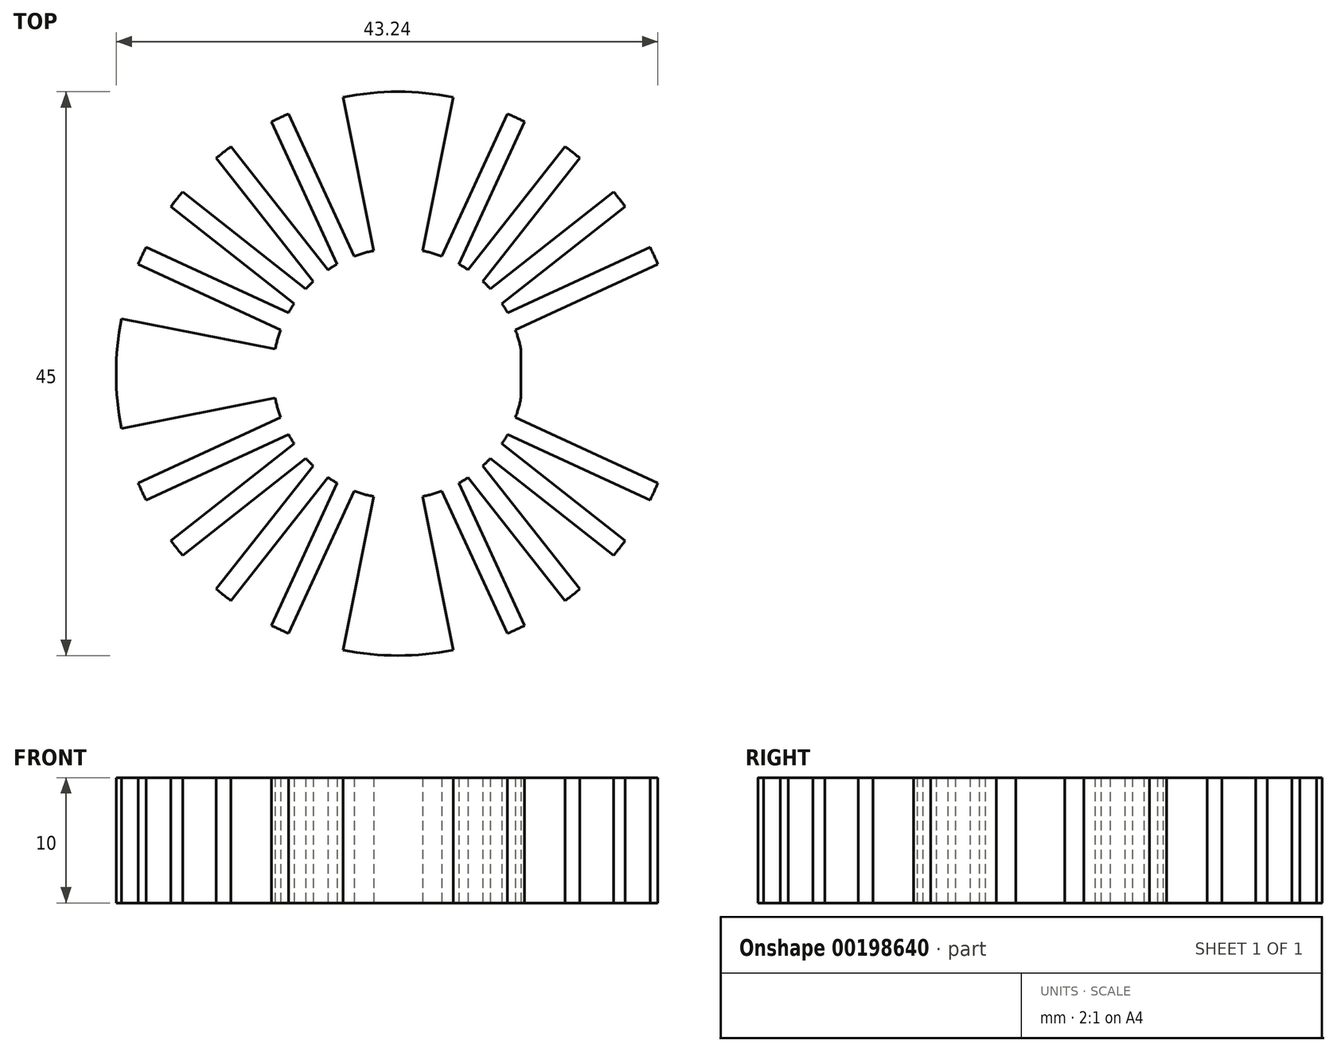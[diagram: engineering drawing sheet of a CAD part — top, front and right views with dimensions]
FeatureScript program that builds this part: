
annotation { "Feature Type Name" : "Feature", "Feature Type Description" : "" }
export const myFeature = defineFeature(function(context is Context, id is Id, definition is map)
    precondition{}
    {
        {
            var Q0;
            Q0=qCreatedBy(makeId("Top.planeOp"),FACE);
            var sketch = newSketch(context, id + "F0", { "sketchPlane" : qUnion([Q0])});
            skArc(sketch, "E0", {"start": v(4.39, 22.07) * mm, "mid": v(0, 22.5) * mm, "end": v(-4.39, 22.07) * mm});
            skArc(sketch, "E1", {"start": v(-1.95, 9.8) * mm, "mid": v(-2.73, 9.62) * mm, "end": v(-3.5, 9.37) * mm});
            skLineSegment(sketch, "E2", {"start": v(1.95, 9.8) * mm, "end": v(4.39, 22.07) * mm});
            skLineSegment(sketch, "E3", {"start": v(4.39, 22.07) * mm, "end": v(1.95, 9.8) * mm});
            skLineSegment(sketch, "E4", {"start": v(-1.95, 9.8) * mm, "end": v(-4.39, 22.07) * mm});
            skLineSegment(sketch, "E5.1.0", {"start": v(-22.07, 4.39) * mm, "end": v(-9.8, 1.95) * mm});
            skLineSegment(sketch, "E5.1.1", {"start": v(-9.8, -1.95) * mm, "end": v(-22.07, -4.39) * mm});
            skLineSegment(sketch, "E5.2.0", {"start": v(-4.39, -22.07) * mm, "end": v(-1.95, -9.8) * mm});
            skLineSegment(sketch, "E5.2.1", {"start": v(1.95, -9.8) * mm, "end": v(4.39, -22.07) * mm});
            skLineSegment(sketch, "E5.3.0", {"start": v(22.07, -4.39) * mm, "end": v(9.8, -1.95) * mm});
            skLineSegment(sketch, "E5.3.1", {"start": v(9.8, 1.95) * mm, "end": v(22.07, 4.39) * mm});
            skLineSegment(sketch, "E6", {"start": v(0, 0) * mm, "end": v(9.42, 20.43) * mm, "construction": true});
            skLineSegment(sketch, "E7", {"start": v(9.42, 20.43) * mm, "end": v(13.93, 17.67) * mm, "construction": true});
            skLineSegment(sketch, "E8", {"start": v(13.93, 17.67) * mm, "end": v(0, 0) * mm, "construction": true});
            skLineSegment(sketch, "E9", {"start": v(4.39, 22.07) * mm, "end": v(9.42, 20.43) * mm, "construction": true});
            skLineSegment(sketch, "E10", {"start": v(0, 0) * mm, "end": v(17.67, 13.93) * mm, "construction": true});
            skLineSegment(sketch, "E11", {"start": v(17.67, 13.93) * mm, "end": v(13.93, 17.67) * mm, "construction": true});
            skLineSegment(sketch, "E12", {"start": v(0, 0) * mm, "end": v(20.43, 9.42) * mm, "construction": true});
            skLineSegment(sketch, "E13", {"start": v(20.43, 9.42) * mm, "end": v(17.67, 13.93) * mm, "construction": true});
            skLineSegment(sketch, "E14", {"start": v(20.43, 9.42) * mm, "end": v(22.07, 4.39) * mm, "construction": true});
            skLineSegment(sketch, "E15", {"start": v(3.5, 9.37) * mm, "end": v(8.73, 20.74) * mm});
            skLineSegment(sketch, "E16.MirrorCS", {"start": v(4.86, 8.74) * mm, "end": v(10.1, 20.1) * mm});
            skLineSegment(sketch, "E17.1.0", {"start": v(5.58, 8.3) * mm, "end": v(13.33, 18.12) * mm});
            skLineSegment(sketch, "E17.1.1", {"start": v(6.76, 7.37) * mm, "end": v(14.51, 17.2) * mm});
            skLineSegment(sketch, "E17.2.0", {"start": v(7.37, 6.76) * mm, "end": v(17.2, 14.51) * mm});
            skLineSegment(sketch, "E17.2.1", {"start": v(8.3, 5.58) * mm, "end": v(18.12, 13.33) * mm});
            skLineSegment(sketch, "E17.3.0", {"start": v(8.74, 4.86) * mm, "end": v(20.1, 10.1) * mm});
            skLineSegment(sketch, "E17.3.1", {"start": v(9.37, 3.5) * mm, "end": v(20.74, 8.73) * mm});
            skLineSegment(sketch, "E17.anchor1", {"start": v(0, 0) * mm, "end": v(3.5, 9.37) * mm, "construction": true});
            skLineSegment(sketch, "E17.anchor2", {"start": v(0, 0) * mm, "end": v(8.74, 4.86) * mm, "construction": true});
            skArc(sketch, "E18.trimOffspring", {"start": v(10.1, 20.1) * mm, "mid": v(9.42, 20.43) * mm, "end": v(8.73, 20.74) * mm});
            skArc(sketch, "E19.trimOffspring", {"start": v(14.51, 17.2) * mm, "mid": v(13.93, 17.67) * mm, "end": v(13.33, 18.12) * mm});
            skArc(sketch, "E20.trimOffspring", {"start": v(18.12, 13.33) * mm, "mid": v(17.67, 13.93) * mm, "end": v(17.2, 14.51) * mm});
            skArc(sketch, "E21.trimOffspring", {"start": v(20.74, 8.73) * mm, "mid": v(20.43, 9.42) * mm, "end": v(20.1, 10.1) * mm});
            skLineSegment(sketch, "E22.1.0", {"start": v(-9.37, 3.5) * mm, "end": v(-20.74, 8.73) * mm});
            skLineSegment(sketch, "E22.1.1", {"start": v(-8.74, 4.86) * mm, "end": v(-20.1, 10.1) * mm});
            skLineSegment(sketch, "E22.1.2", {"start": v(-8.3, 5.58) * mm, "end": v(-18.12, 13.33) * mm});
            skLineSegment(sketch, "E22.1.3", {"start": v(-7.37, 6.76) * mm, "end": v(-17.2, 14.51) * mm});
            skLineSegment(sketch, "E22.1.4", {"start": v(-6.76, 7.37) * mm, "end": v(-14.51, 17.2) * mm});
            skLineSegment(sketch, "E22.1.5", {"start": v(-5.58, 8.3) * mm, "end": v(-13.33, 18.12) * mm});
            skLineSegment(sketch, "E22.1.6", {"start": v(-4.86, 8.74) * mm, "end": v(-10.1, 20.1) * mm});
            skLineSegment(sketch, "E22.1.7", {"start": v(-3.5, 9.37) * mm, "end": v(-8.73, 20.74) * mm});
            skLineSegment(sketch, "E22.2.0", {"start": v(-3.5, -9.37) * mm, "end": v(-8.73, -20.74) * mm});
            skLineSegment(sketch, "E22.2.1", {"start": v(-4.86, -8.74) * mm, "end": v(-10.1, -20.1) * mm});
            skLineSegment(sketch, "E22.2.2", {"start": v(-5.58, -8.3) * mm, "end": v(-13.33, -18.12) * mm});
            skLineSegment(sketch, "E22.2.3", {"start": v(-6.76, -7.37) * mm, "end": v(-14.51, -17.2) * mm});
            skLineSegment(sketch, "E22.2.4", {"start": v(-7.37, -6.76) * mm, "end": v(-17.2, -14.51) * mm});
            skLineSegment(sketch, "E22.2.5", {"start": v(-8.3, -5.58) * mm, "end": v(-18.12, -13.33) * mm});
            skLineSegment(sketch, "E22.2.6", {"start": v(-8.74, -4.86) * mm, "end": v(-20.1, -10.1) * mm});
            skLineSegment(sketch, "E22.2.7", {"start": v(-9.37, -3.5) * mm, "end": v(-20.74, -8.73) * mm});
            skLineSegment(sketch, "E22.3.0", {"start": v(9.37, -3.5) * mm, "end": v(20.74, -8.73) * mm});
            skLineSegment(sketch, "E22.3.1", {"start": v(8.74, -4.86) * mm, "end": v(20.1, -10.1) * mm});
            skLineSegment(sketch, "E22.3.2", {"start": v(8.3, -5.58) * mm, "end": v(18.12, -13.33) * mm});
            skLineSegment(sketch, "E22.3.3", {"start": v(7.37, -6.76) * mm, "end": v(17.2, -14.51) * mm});
            skLineSegment(sketch, "E22.3.4", {"start": v(6.76, -7.37) * mm, "end": v(14.51, -17.2) * mm});
            skLineSegment(sketch, "E22.3.5", {"start": v(5.58, -8.3) * mm, "end": v(13.33, -18.12) * mm});
            skLineSegment(sketch, "E22.3.6", {"start": v(4.86, -8.74) * mm, "end": v(10.1, -20.1) * mm});
            skLineSegment(sketch, "E22.3.7", {"start": v(3.5, -9.37) * mm, "end": v(8.73, -20.74) * mm});
            skArc(sketch, "E23.trimOffspring", {"start": v(22.07, -4.39) * mm, "mid": v(22.5, 0) * mm, "end": v(22.07, 4.39) * mm});
            skArc(sketch, "E24.trimOffspring", {"start": v(20.1, -10.1) * mm, "mid": v(20.43, -9.42) * mm, "end": v(20.74, -8.73) * mm});
            skArc(sketch, "E25.trimOffspring", {"start": v(17.2, -14.51) * mm, "mid": v(17.67, -13.93) * mm, "end": v(18.12, -13.33) * mm});
            skArc(sketch, "E26.trimOffspring", {"start": v(13.33, -18.12) * mm, "mid": v(13.93, -17.67) * mm, "end": v(14.51, -17.2) * mm});
            skArc(sketch, "E27.trimOffspring", {"start": v(8.73, -20.74) * mm, "mid": v(9.42, -20.43) * mm, "end": v(10.1, -20.1) * mm});
            skArc(sketch, "E28.trimOffspring", {"start": v(-4.39, -22.07) * mm, "mid": v(0, -22.5) * mm, "end": v(4.39, -22.07) * mm});
            skArc(sketch, "E29.trimOffspring", {"start": v(-10.1, -20.1) * mm, "mid": v(-9.42, -20.43) * mm, "end": v(-8.73, -20.74) * mm});
            skArc(sketch, "E30.trimOffspring", {"start": v(-14.51, -17.2) * mm, "mid": v(-13.93, -17.67) * mm, "end": v(-13.33, -18.12) * mm});
            skArc(sketch, "E31.trimOffspring", {"start": v(-18.12, -13.33) * mm, "mid": v(-17.67, -13.93) * mm, "end": v(-17.2, -14.51) * mm});
            skArc(sketch, "E32.trimOffspring", {"start": v(-20.74, -8.73) * mm, "mid": v(-20.43, -9.42) * mm, "end": v(-20.1, -10.1) * mm});
            skArc(sketch, "E33.trimOffspring", {"start": v(-22.07, 4.39) * mm, "mid": v(-22.5, 0) * mm, "end": v(-22.07, -4.39) * mm});
            skArc(sketch, "E34.trimOffspring", {"start": v(-20.1, 10.1) * mm, "mid": v(-20.43, 9.42) * mm, "end": v(-20.74, 8.73) * mm});
            skArc(sketch, "E35.trimOffspring", {"start": v(-17.2, 14.51) * mm, "mid": v(-17.67, 13.93) * mm, "end": v(-18.12, 13.33) * mm});
            skArc(sketch, "E36.trimOffspring", {"start": v(-13.33, 18.12) * mm, "mid": v(-13.93, 17.67) * mm, "end": v(-14.51, 17.2) * mm});
            skArc(sketch, "E37.trimOffspring", {"start": v(-8.73, 20.74) * mm, "mid": v(-9.42, 20.43) * mm, "end": v(-10.1, 20.1) * mm});
            skArc(sketch, "E38.trimOffspring", {"start": v(-4.86, 8.74) * mm, "mid": v(-5.22, 8.53) * mm, "end": v(-5.58, 8.3) * mm});
            skArc(sketch, "E39.trimOffspring", {"start": v(-6.76, 7.37) * mm, "mid": v(-7.07, 7.07) * mm, "end": v(-7.37, 6.76) * mm});
            skArc(sketch, "E40.trimOffspring", {"start": v(-8.3, 5.58) * mm, "mid": v(-8.53, 5.22) * mm, "end": v(-8.74, 4.86) * mm});
            skArc(sketch, "E41.trimOffspring", {"start": v(-9.37, 3.5) * mm, "mid": v(-9.62, 2.73) * mm, "end": v(-9.8, 1.95) * mm});
            skArc(sketch, "E42.trimOffspring", {"start": v(-9.8, -1.95) * mm, "mid": v(-9.62, -2.73) * mm, "end": v(-9.37, -3.5) * mm});
            skArc(sketch, "E43.trimOffspring", {"start": v(-8.74, -4.86) * mm, "mid": v(-8.53, -5.22) * mm, "end": v(-8.3, -5.58) * mm});
            skArc(sketch, "E44.trimOffspring", {"start": v(-7.37, -6.76) * mm, "mid": v(-7.07, -7.07) * mm, "end": v(-6.76, -7.37) * mm});
            skArc(sketch, "E45.trimOffspring", {"start": v(-5.58, -8.3) * mm, "mid": v(-5.22, -8.53) * mm, "end": v(-4.86, -8.74) * mm});
            skArc(sketch, "E46.trimOffspring", {"start": v(-3.5, -9.37) * mm, "mid": v(-2.73, -9.62) * mm, "end": v(-1.95, -9.8) * mm});
            skArc(sketch, "E47.trimOffspring", {"start": v(1.95, -9.8) * mm, "mid": v(2.73, -9.62) * mm, "end": v(3.5, -9.37) * mm});
            skArc(sketch, "E48.trimOffspring", {"start": v(4.86, -8.74) * mm, "mid": v(5.22, -8.53) * mm, "end": v(5.58, -8.3) * mm});
            skArc(sketch, "E49.trimOffspring", {"start": v(6.76, -7.37) * mm, "mid": v(7.07, -7.07) * mm, "end": v(7.37, -6.76) * mm});
            skArc(sketch, "E50.trimOffspring", {"start": v(8.3, -5.58) * mm, "mid": v(8.53, -5.22) * mm, "end": v(8.74, -4.86) * mm});
            skArc(sketch, "E51.trimOffspring", {"start": v(9.37, -3.5) * mm, "mid": v(9.62, -2.73) * mm, "end": v(9.8, -1.95) * mm});
            skArc(sketch, "E52.trimOffspring", {"start": v(9.8, 1.95) * mm, "mid": v(9.62, 2.73) * mm, "end": v(9.37, 3.5) * mm});
            skArc(sketch, "E53.trimOffspring", {"start": v(8.74, 4.86) * mm, "mid": v(8.53, 5.22) * mm, "end": v(8.3, 5.58) * mm});
            skArc(sketch, "E54.trimOffspring", {"start": v(7.37, 6.76) * mm, "mid": v(7.07, 7.07) * mm, "end": v(6.76, 7.37) * mm});
            skArc(sketch, "E55.trimOffspring", {"start": v(5.58, 8.3) * mm, "mid": v(5.22, 8.53) * mm, "end": v(4.86, 8.74) * mm});
            skArc(sketch, "E56.trimOffspring", {"start": v(3.5, 9.37) * mm, "mid": v(2.73, 9.62) * mm, "end": v(1.95, 9.8) * mm});
            skSolve(sketch);
        }
        {
            var Q0;
            Q0 = qSketchRegion(id + "F0", true);
            extrude(context, id + "F1", {"entities" : qUnion([Q0]), "depth" : 10 * mm});
        }
        {
            var Q0;
            Q0=makeQuery(id+"F1.opExtrude","CAP_FACE",FACE,{"disambiguationData":[OSD([sQuery(id+"F0.wireOp",EDGE,"E0"),sQuery(id+"F0.wireOp",EDGE,"E1"),sQuery(id+"F0.wireOp",EDGE,"E3"),sQuery(id+"F0.wireOp",EDGE,"E4"),sQuery(id+"F0.wireOp",EDGE,"E5.1.0"),sQuery(id+"F0.wireOp",EDGE,"E5.1.1"),sQuery(id+"F0.wireOp",EDGE,"E5.2.0"),sQuery(id+"F0.wireOp",EDGE,"E5.2.1"),sQuery(id+"F0.wireOp",EDGE,"E5.3.0"),sQuery(id+"F0.wireOp",EDGE,"E5.3.1"),sQuery(id+"F0.wireOp",EDGE,"E15"),sQuery(id+"F0.wireOp",EDGE,"E16.MirrorCS"),sQuery(id+"F0.wireOp",EDGE,"E17.1.0"),sQuery(id+"F0.wireOp",EDGE,"E17.1.1"),sQuery(id+"F0.wireOp",EDGE,"E17.2.0"),sQuery(id+"F0.wireOp",EDGE,"E17.2.1"),sQuery(id+"F0.wireOp",EDGE,"E17.3.0"),sQuery(id+"F0.wireOp",EDGE,"E17.3.1"),sQuery(id+"F0.wireOp",EDGE,"E18.trimOffspring"),sQuery(id+"F0.wireOp",EDGE,"E19.trimOffspring"),sQuery(id+"F0.wireOp",EDGE,"E20.trimOffspring"),sQuery(id+"F0.wireOp",EDGE,"E21.trimOffspring"),sQuery(id+"F0.wireOp",EDGE,"E22.1.0"),sQuery(id+"F0.wireOp",EDGE,"E22.1.1"),sQuery(id+"F0.wireOp",EDGE,"E22.1.2"),sQuery(id+"F0.wireOp",EDGE,"E22.1.3"),sQuery(id+"F0.wireOp",EDGE,"E22.1.4"),sQuery(id+"F0.wireOp",EDGE,"E22.1.5"),sQuery(id+"F0.wireOp",EDGE,"E22.1.6"),sQuery(id+"F0.wireOp",EDGE,"E22.1.7"),sQuery(id+"F0.wireOp",EDGE,"E22.2.0"),sQuery(id+"F0.wireOp",EDGE,"E22.2.1"),sQuery(id+"F0.wireOp",EDGE,"E22.2.2"),sQuery(id+"F0.wireOp",EDGE,"E22.2.3"),sQuery(id+"F0.wireOp",EDGE,"E22.2.4"),sQuery(id+"F0.wireOp",EDGE,"E22.2.5"),sQuery(id+"F0.wireOp",EDGE,"E22.2.6"),sQuery(id+"F0.wireOp",EDGE,"E22.2.7"),sQuery(id+"F0.wireOp",EDGE,"E22.3.0"),sQuery(id+"F0.wireOp",EDGE,"E22.3.1"),sQuery(id+"F0.wireOp",EDGE,"E22.3.2"),sQuery(id+"F0.wireOp",EDGE,"E22.3.3"),sQuery(id+"F0.wireOp",EDGE,"E22.3.4"),sQuery(id+"F0.wireOp",EDGE,"E22.3.5"),sQuery(id+"F0.wireOp",EDGE,"E22.3.6"),sQuery(id+"F0.wireOp",EDGE,"E22.3.7"),sQuery(id+"F0.wireOp",EDGE,"E23.trimOffspring"),sQuery(id+"F0.wireOp",EDGE,"E24.trimOffspring"),sQuery(id+"F0.wireOp",EDGE,"E25.trimOffspring"),sQuery(id+"F0.wireOp",EDGE,"E26.trimOffspring"),sQuery(id+"F0.wireOp",EDGE,"E27.trimOffspring"),sQuery(id+"F0.wireOp",EDGE,"E28.trimOffspring"),sQuery(id+"F0.wireOp",EDGE,"E29.trimOffspring"),sQuery(id+"F0.wireOp",EDGE,"E30.trimOffspring"),sQuery(id+"F0.wireOp",EDGE,"E31.trimOffspring"),sQuery(id+"F0.wireOp",EDGE,"E32.trimOffspring"),sQuery(id+"F0.wireOp",EDGE,"E33.trimOffspring"),sQuery(id+"F0.wireOp",EDGE,"E34.trimOffspring"),sQuery(id+"F0.wireOp",EDGE,"E35.trimOffspring"),sQuery(id+"F0.wireOp",EDGE,"E36.trimOffspring"),sQuery(id+"F0.wireOp",EDGE,"E37.trimOffspring"),sQuery(id+"F0.wireOp",EDGE,"E38.trimOffspring"),sQuery(id+"F0.wireOp",EDGE,"E39.trimOffspring"),sQuery(id+"F0.wireOp",EDGE,"E40.trimOffspring"),sQuery(id+"F0.wireOp",EDGE,"E41.trimOffspring"),sQuery(id+"F0.wireOp",EDGE,"E42.trimOffspring"),sQuery(id+"F0.wireOp",EDGE,"E43.trimOffspring"),sQuery(id+"F0.wireOp",EDGE,"E44.trimOffspring"),sQuery(id+"F0.wireOp",EDGE,"E45.trimOffspring"),sQuery(id+"F0.wireOp",EDGE,"E46.trimOffspring"),sQuery(id+"F0.wireOp",EDGE,"E47.trimOffspring"),sQuery(id+"F0.wireOp",EDGE,"E48.trimOffspring"),sQuery(id+"F0.wireOp",EDGE,"E49.trimOffspring"),sQuery(id+"F0.wireOp",EDGE,"E50.trimOffspring"),sQuery(id+"F0.wireOp",EDGE,"E51.trimOffspring"),sQuery(id+"F0.wireOp",EDGE,"E52.trimOffspring"),sQuery(id+"F0.wireOp",EDGE,"E53.trimOffspring"),sQuery(id+"F0.wireOp",EDGE,"E54.trimOffspring"),sQuery(id+"F0.wireOp",EDGE,"E55.trimOffspring"),sQuery(id+"F0.wireOp",EDGE,"E56.trimOffspring")])],"isStart":false});
            var sketch = newSketch(context, id + "F2", { "sketchPlane" : qUnion([Q0])});
            skLineSegment(sketch, "E57", {"start": v(9.8, 1.95) * mm, "end": v(9.8, -1.95) * mm});
            skLineSegment(sketch, "E58.0", {"start": v(22.07, -4.39) * mm, "end": v(9.8, -1.95) * mm});
            skLineSegment(sketch, "E58.1", {"start": v(9.8, 1.95) * mm, "end": v(22.07, 4.39) * mm});
            skArc(sketch, "E58.2", {"start": v(22.07, -4.39) * mm, "mid": v(22.5, 0) * mm, "end": v(22.07, 4.39) * mm});
            skSolve(sketch);
        }
        {
            var Q0;
            Q0 = qSketchRegion(id + "F2", true);
            extrude(context, id + "F3", {"entities" : qUnion([Q0]), "operationType" : NewBodyOperationType.REMOVE, "endBound" : BoundingType.THROUGH_ALL, "oppositeDirection" : true, "depth" : 25 * mm});
        }
    });
